# Revit family: Shower-Shower_Trim-KOHLER-Forte-K-TLS10276
name_source: partatom
category: Plumbing Fixtures
revit_build: Autodesk Revit 2015 (Build: 20140606_1530(x64)
units: mm (PartAtom-declared; Revit-internal decimal feet)

## types (6) — shared parameters
ADA Compliant = Yes
Assembly Code = D2010700
CW Connection = No
Cold Water Inlet = Cold Water Inlet
Date Modified = 5/06/2019
Default Elevation = 42"
Drain Included = No
Flow Rate = 0 GPM
HW Connection = Yes
Height = 6 3/8"
Hot Water Inlet = Tempered Water Inlet
Length = 4 1/2"
Manufacturer = KOHLER Co.
MasterFormat 1995 = 15410
MasterFormat 2004 = 22.41.23
Material = Premium Metal Construction
Pressure = 0.00 psi
Product Documentation Link = https://www.us.kohler.com
Product Name = Forte
Product Page URL = http://www.us.kohler.com
URL = https://www.us.kohler.com
Vent Connection = No
Waste Connection = No
Waste Water Outlet = Waste Water Outlet
WaterSense Certified = No
Width = 6 3/8"

## per-type parameters (varying)
| type | Description | Finish | Model | Sculpted Lever Handle | Traditional Lever Handle | Type |
| Sculpted Lever Handle,CP-Polished Chrome | Sculpted Rite-Temp shower valve trim, less showerhead | Kohler-Metal-CP-Polished_Chrome | K-TLS10276-4-CP | Yes | No | 1 |
| Sculpted Lever Handle,G-Brushed Chrome | Sculpted Rite-Temp shower valve trim, less showerhead | Kohler-Metal-G-Brushed_Chrome | K-TLS10276-4-G | Yes | No | 2 |
| Sculpted Lever Handle,BN-Vibrant Brushed Nickel | Sculpted Rite-Temp shower valve trim, less showerhead | Kohler-Metal-BN-Vibrant_Brushed_Nickel | K-TLS10276-4-BN | Yes | No | 3 |
| Traditional Lever Handle,CP-Polished Chrome | Traditional Rite-Temp shower valve trim, less showerhead | Kohler-Metal-CP-Polished_Chrome | K-TLS10276-4A-CP | No | Yes | 4 |
| Traditional Lever Handle,G-Brushed Chrome | Traditional Rite-Temp shower valve trim, less showerhead | Kohler-Metal-G-Brushed_Chrome | K-TLS10276-4A-G | No | Yes | 5 |
| Traditional Lever Handle,BN-Vibrant Brushed Nickel | Traditional Rite-Temp shower valve trim, less showerhead | Kohler-Metal-BN-Vibrant_Brushed_Nickel | K-TLS10276-4A-BN | No | Yes | 6 |

## geometry (parser evidence)
native form markers: Sweep x7
no freeform markers — native parametric forms only
